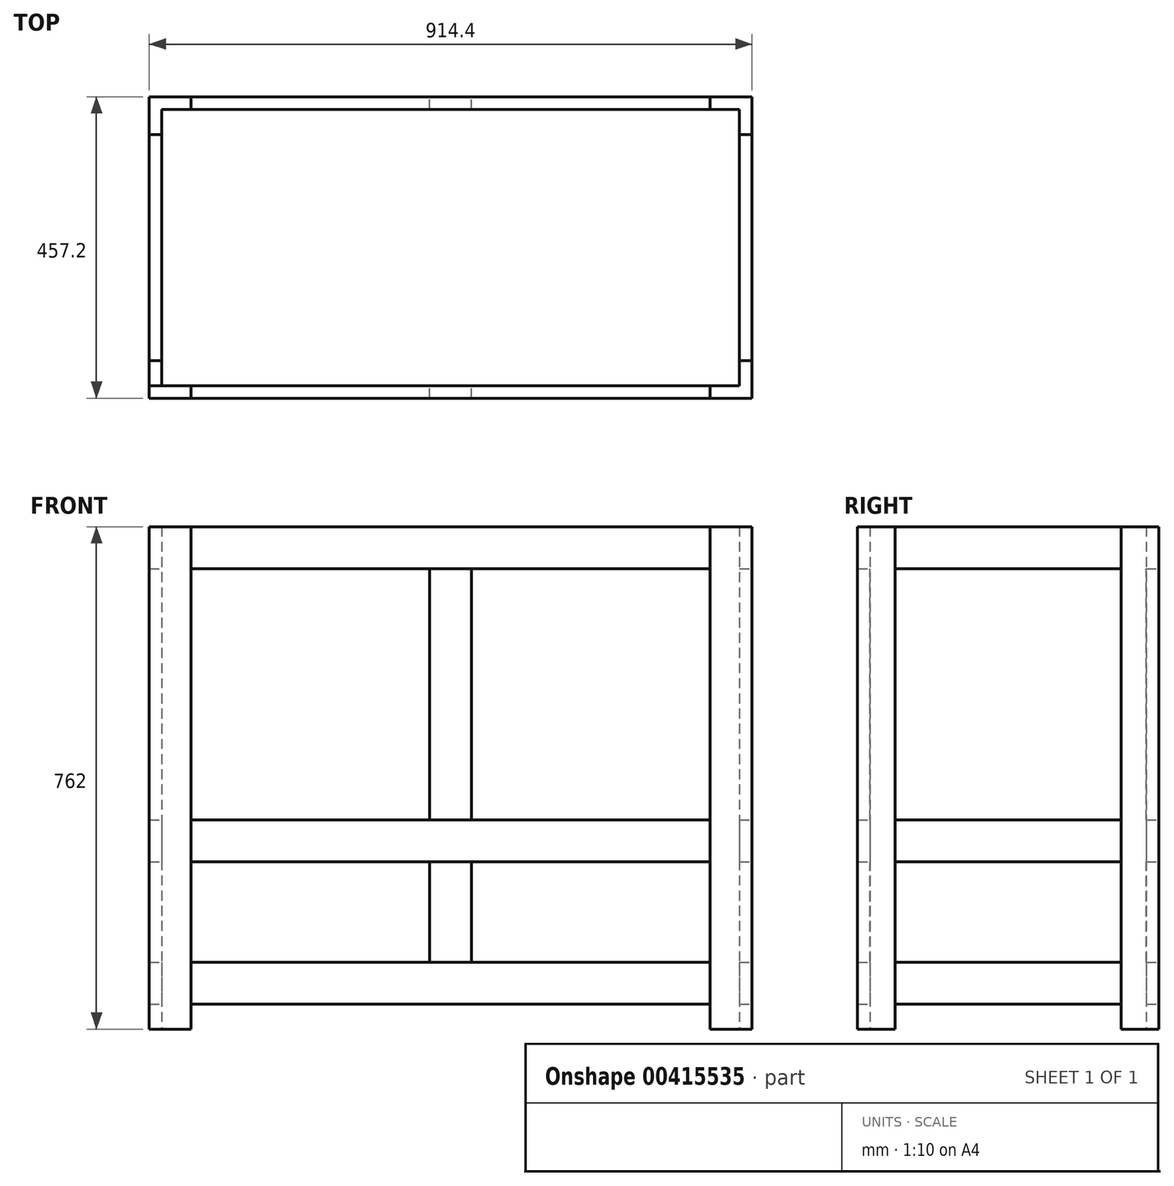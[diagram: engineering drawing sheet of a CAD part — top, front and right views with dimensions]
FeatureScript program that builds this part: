
annotation { "Feature Type Name" : "Feature", "Feature Type Description" : "" }
export const myFeature = defineFeature(function(context is Context, id is Id, definition is map)
    precondition{}
    {
        {
            var Q0;
            Q0=qCreatedBy(makeId("Top.planeOp"),FACE);
            var sketch = newSketch(context, id + "F0", { "sketchPlane" : qUnion([Q0])});
            skLineSegment(sketch, "E0.bottom", {"start": v(0, 0) * mm, "end": v(63.5, 0) * mm});
            skLineSegment(sketch, "E0.top", {"start": v(0, -19.05) * mm, "end": v(63.5, -19.05) * mm});
            skLineSegment(sketch, "E0.left", {"start": v(0, 0) * mm, "end": v(0, -19.05) * mm});
            skLineSegment(sketch, "E0.right", {"start": v(63.5, 0) * mm, "end": v(63.5, -19.05) * mm});
            skSolve(sketch);
        }
        {
            var Q0;
            Q0 = qSketchRegion(id + "F0", true);
            extrude(context, id + "F1", {"entities" : qUnion([Q0]), "depth" : 762 * mm});
        }
        {
            var Q0;
            Q0=qCreatedBy(makeId("Top.planeOp"),FACE);
            var sketch = newSketch(context, id + "F2", { "sketchPlane" : qUnion([Q0])});
            skLineSegment(sketch, "E1.bottom", {"start": v(0, -19.05) * mm, "end": v(19.05, -19.05) * mm});
            skLineSegment(sketch, "E1.top", {"start": v(0, -57.15) * mm, "end": v(19.05, -57.15) * mm});
            skLineSegment(sketch, "E1.left", {"start": v(0, -19.05) * mm, "end": v(0, -57.15) * mm});
            skLineSegment(sketch, "E1.right", {"start": v(19.05, -19.05) * mm, "end": v(19.05, -57.15) * mm});
            skSolve(sketch);
        }
        {
            var Q0;
            Q0 = qSketchRegion(id + "F2", true);
            extrude(context, id + "F3", {"entities" : qUnion([Q0]), "operationType" : NewBodyOperationType.ADD, "depth" : 762 * mm});
        }
        {
            var Q0;
            Q0=qCreatedBy(makeId("Top.planeOp"),FACE);
            var sketch = newSketch(context, id + "F4", { "sketchPlane" : qUnion([Q0])});
            skLineSegment(sketch, "E2.bottom", {"start": v(0, -438.15) * mm, "end": v(63.5, -438.15) * mm});
            skLineSegment(sketch, "E2.top", {"start": v(0, -457.2) * mm, "end": v(63.5, -457.2) * mm});
            skLineSegment(sketch, "E2.left", {"start": v(0, -438.15) * mm, "end": v(0, -457.2) * mm});
            skLineSegment(sketch, "E2.right", {"start": v(63.5, -438.15) * mm, "end": v(63.5, -457.2) * mm});
            skSolve(sketch);
        }
        {
            var Q0;
            Q0=qCreatedBy(makeId("Top.planeOp"),FACE);
            var sketch = newSketch(context, id + "F5", { "sketchPlane" : qUnion([Q0])});
            skLineSegment(sketch, "E3.bottom", {"start": v(19.05, -400.05) * mm, "end": v(0, -400.05) * mm});
            skLineSegment(sketch, "E3.top", {"start": v(19.05, -438.15) * mm, "end": v(0, -438.15) * mm});
            skLineSegment(sketch, "E3.left", {"start": v(19.05, -400.05) * mm, "end": v(19.05, -438.15) * mm});
            skLineSegment(sketch, "E3.right", {"start": v(0, -400.05) * mm, "end": v(0, -438.15) * mm});
            skSolve(sketch);
        }
        {
            var Q0;
            Q0=qCreatedBy(makeId("Top.planeOp"),FACE);
            var sketch = newSketch(context, id + "F6", { "sketchPlane" : qUnion([Q0])});
            skLineSegment(sketch, "E4.bottom", {"start": v(850.9, 0) * mm, "end": v(914.4, 0) * mm});
            skLineSegment(sketch, "E4.top", {"start": v(850.9, -19.05) * mm, "end": v(914.4, -19.05) * mm});
            skLineSegment(sketch, "E4.left", {"start": v(850.9, 0) * mm, "end": v(850.9, -19.05) * mm});
            skLineSegment(sketch, "E4.right", {"start": v(914.4, 0) * mm, "end": v(914.4, -19.05) * mm});
            skSolve(sketch);
        }
        {
            var Q0;
            Q0=qCreatedBy(makeId("Top.planeOp"),FACE);
            var sketch = newSketch(context, id + "F7", { "sketchPlane" : qUnion([Q0])});
            skLineSegment(sketch, "E5.bottom", {"start": v(895.35, -57.15) * mm, "end": v(914.4, -57.15) * mm});
            skLineSegment(sketch, "E5.top", {"start": v(895.35, -19.05) * mm, "end": v(914.4, -19.05) * mm});
            skLineSegment(sketch, "E5.left", {"start": v(895.35, -57.15) * mm, "end": v(895.35, -19.05) * mm});
            skLineSegment(sketch, "E5.right", {"start": v(914.4, -57.15) * mm, "end": v(914.4, -19.05) * mm});
            skSolve(sketch);
        }
        {
            var Q0;
            Q0=qCreatedBy(makeId("Top.planeOp"),FACE);
            var sketch = newSketch(context, id + "F8", { "sketchPlane" : qUnion([Q0])});
            skLineSegment(sketch, "E6.bottom", {"start": v(850.9, -457.2) * mm, "end": v(914.4, -457.2) * mm});
            skLineSegment(sketch, "E6.top", {"start": v(850.9, -438.15) * mm, "end": v(914.4, -438.15) * mm});
            skLineSegment(sketch, "E6.left", {"start": v(850.9, -457.2) * mm, "end": v(850.9, -438.15) * mm});
            skLineSegment(sketch, "E6.right", {"start": v(914.4, -457.2) * mm, "end": v(914.4, -438.15) * mm});
            skSolve(sketch);
        }
        {
            var Q0;
            Q0=qCreatedBy(makeId("Top.planeOp"),FACE);
            var sketch = newSketch(context, id + "F9", { "sketchPlane" : qUnion([Q0])});
            skLineSegment(sketch, "E7.bottom", {"start": v(895.35, -400.05) * mm, "end": v(914.4, -400.05) * mm});
            skLineSegment(sketch, "E7.top", {"start": v(895.35, -438.15) * mm, "end": v(914.4, -438.15) * mm});
            skLineSegment(sketch, "E7.left", {"start": v(895.35, -400.05) * mm, "end": v(895.35, -438.15) * mm});
            skLineSegment(sketch, "E7.right", {"start": v(914.4, -400.05) * mm, "end": v(914.4, -438.15) * mm});
            skSolve(sketch);
        }
        {
            var Q0;
            Q0 = qSketchRegion(id + "F4", true);
            extrude(context, id + "F10", {"entities" : qUnion([Q0]), "depth" : 762 * mm});
        }
        {
            var Q0;
            Q0 = qSketchRegion(id + "F5", true);
            extrude(context, id + "F11", {"entities" : qUnion([Q0]), "depth" : 762 * mm});
        }
        {
            var Q0;
            Q0 = qSketchRegion(id + "F6", true);
            extrude(context, id + "F12", {"entities" : qUnion([Q0]), "depth" : 762 * mm});
        }
        {
            var Q0;
            Q0 = qSketchRegion(id + "F7", true);
            extrude(context, id + "F13", {"entities" : qUnion([Q0]), "operationType" : NewBodyOperationType.ADD, "depth" : 762 * mm});
        }
        {
            var Q0;
            Q0 = qSketchRegion(id + "F8", true);
            extrude(context, id + "F14", {"entities" : qUnion([Q0]), "depth" : 762 * mm});
        }
        {
            var Q0;
            Q0 = qSketchRegion(id + "F9", true);
            extrude(context, id + "F15", {"entities" : qUnion([Q0]), "operationType" : NewBodyOperationType.ADD, "depth" : 762 * mm});
        }
        {
            var Q0;
            Q0=makeQuery(id+"F10.opExtrude","SWEPT_FACE",FACE,{"disambiguationData":[OSD([sQuery(id+"F4.wireOp",EDGE,"E2.right")])]});
            var sketch = newSketch(context, id + "F16", { "sketchPlane" : qUnion([Q0])});
            skLineSegment(sketch, "E8.bottom", {"start": v(-457.2, 762) * mm, "end": v(-438.15, 762) * mm});
            skLineSegment(sketch, "E8.top", {"start": v(-457.2, 698.5) * mm, "end": v(-438.15, 698.5) * mm});
            skLineSegment(sketch, "E8.left", {"start": v(-457.2, 762) * mm, "end": v(-457.2, 698.5) * mm});
            skLineSegment(sketch, "E8.right", {"start": v(-438.15, 762) * mm, "end": v(-438.15, 698.5) * mm});
            skLineSegment(sketch, "E9.bottom", {"start": v(-457.2, 317.5) * mm, "end": v(-438.15, 317.5) * mm});
            skLineSegment(sketch, "E9.top", {"start": v(-457.2, 254) * mm, "end": v(-438.15, 254) * mm});
            skLineSegment(sketch, "E9.left", {"start": v(-457.2, 317.5) * mm, "end": v(-457.2, 254) * mm});
            skLineSegment(sketch, "E9.right", {"start": v(-438.15, 317.5) * mm, "end": v(-438.15, 254) * mm});
            skLineSegment(sketch, "E10.bottom", {"start": v(-457.2, 101.6) * mm, "end": v(-438.15, 101.6) * mm});
            skLineSegment(sketch, "E10.top", {"start": v(-457.2, 38.1) * mm, "end": v(-438.15, 38.1) * mm});
            skLineSegment(sketch, "E10.left", {"start": v(-457.2, 101.6) * mm, "end": v(-457.2, 38.1) * mm});
            skLineSegment(sketch, "E10.right", {"start": v(-438.15, 101.6) * mm, "end": v(-438.15, 38.1) * mm});
            skSolve(sketch);
        }
        {
            var Q0;
            Q0 = qSketchRegion(id + "F16", true);
            extrude(context, id + "F17", {"entities" : qUnion([Q0]), "depth" : 787.4 * mm});
        }
        {
            var Q0;
            Q0=makeQuery(id+"F1.opExtrude","SWEPT_FACE",FACE,{"disambiguationData":[OSD([sQuery(id+"F0.wireOp",EDGE,"E0.right")])]});
            var sketch = newSketch(context, id + "F18", { "sketchPlane" : qUnion([Q0])});
            skLineSegment(sketch, "E11.bottom", {"start": v(-19.05, 762) * mm, "end": v(0, 762) * mm});
            skLineSegment(sketch, "E11.top", {"start": v(-19.05, 698.5) * mm, "end": v(0, 698.5) * mm});
            skLineSegment(sketch, "E11.left", {"start": v(-19.05, 762) * mm, "end": v(-19.05, 698.5) * mm});
            skLineSegment(sketch, "E11.right", {"start": v(0, 762) * mm, "end": v(0, 698.5) * mm});
            skLineSegment(sketch, "E12.bottom", {"start": v(-19.05, 317.5) * mm, "end": v(0, 317.5) * mm});
            skLineSegment(sketch, "E12.top", {"start": v(-19.05, 254) * mm, "end": v(0, 254) * mm});
            skLineSegment(sketch, "E12.left", {"start": v(-19.05, 317.5) * mm, "end": v(-19.05, 254) * mm});
            skLineSegment(sketch, "E12.right", {"start": v(0, 317.5) * mm, "end": v(0, 254) * mm});
            skLineSegment(sketch, "E13.bottom", {"start": v(-19.05, 101.6) * mm, "end": v(0, 101.6) * mm});
            skLineSegment(sketch, "E13.top", {"start": v(-19.05, 38.1) * mm, "end": v(0, 38.1) * mm});
            skLineSegment(sketch, "E13.left", {"start": v(-19.05, 101.6) * mm, "end": v(-19.05, 38.1) * mm});
            skLineSegment(sketch, "E13.right", {"start": v(0, 101.6) * mm, "end": v(0, 38.1) * mm});
            skSolve(sketch);
        }
        {
            var Q0;
            Q0 = qSketchRegion(id + "F18", true);
            extrude(context, id + "F19", {"entities" : qUnion([Q0]), "depth" : 787.4 * mm});
        }
        {
            var Q0;
            Q0=makeQuery(id+"F13.opExtrude","SWEPT_FACE",FACE,{"disambiguationData":[OSD([sQuery(id+"F7.wireOp",EDGE,"E5.bottom")])]});
            var sketch = newSketch(context, id + "F20", { "sketchPlane" : qUnion([Q0])});
            skLineSegment(sketch, "E14.bottom", {"start": v(895.35, 762) * mm, "end": v(914.4, 762) * mm});
            skLineSegment(sketch, "E14.top", {"start": v(895.35, 698.5) * mm, "end": v(914.4, 698.5) * mm});
            skLineSegment(sketch, "E14.left", {"start": v(895.35, 762) * mm, "end": v(895.35, 698.5) * mm});
            skLineSegment(sketch, "E14.right", {"start": v(914.4, 762) * mm, "end": v(914.4, 698.5) * mm});
            skLineSegment(sketch, "E15.bottom", {"start": v(895.35, 317.5) * mm, "end": v(914.4, 317.5) * mm});
            skLineSegment(sketch, "E15.top", {"start": v(895.35, 254) * mm, "end": v(914.4, 254) * mm});
            skLineSegment(sketch, "E15.left", {"start": v(895.35, 317.5) * mm, "end": v(895.35, 254) * mm});
            skLineSegment(sketch, "E15.right", {"start": v(914.4, 317.5) * mm, "end": v(914.4, 254) * mm});
            skLineSegment(sketch, "E16.bottom", {"start": v(895.35, 101.6) * mm, "end": v(914.4, 101.6) * mm});
            skLineSegment(sketch, "E16.top", {"start": v(895.35, 38.1) * mm, "end": v(914.4, 38.1) * mm});
            skLineSegment(sketch, "E16.left", {"start": v(895.35, 101.6) * mm, "end": v(895.35, 38.1) * mm});
            skLineSegment(sketch, "E16.right", {"start": v(914.4, 101.6) * mm, "end": v(914.4, 38.1) * mm});
            skSolve(sketch);
        }
        {
            var Q0;
            Q0 = qSketchRegion(id + "F20", true);
            extrude(context, id + "F21", {"entities" : qUnion([Q0]), "depth" : 342.9 * mm});
        }
        {
            var Q0;
            Q0=makeQuery(id+"F3.opExtrude","SWEPT_FACE",FACE,{"disambiguationData":[OSD([sQuery(id+"F2.wireOp",EDGE,"E1.top")])]});
            var sketch = newSketch(context, id + "F22", { "sketchPlane" : qUnion([Q0])});
            skLineSegment(sketch, "E17.bottom", {"start": v(0, 762) * mm, "end": v(19.05, 762) * mm});
            skLineSegment(sketch, "E17.top", {"start": v(0, 698.5) * mm, "end": v(19.05, 698.5) * mm});
            skLineSegment(sketch, "E17.left", {"start": v(0, 762) * mm, "end": v(0, 698.5) * mm});
            skLineSegment(sketch, "E17.right", {"start": v(19.05, 762) * mm, "end": v(19.05, 698.5) * mm});
            skLineSegment(sketch, "E18.bottom", {"start": v(0, 317.5) * mm, "end": v(19.05, 317.5) * mm});
            skLineSegment(sketch, "E18.top", {"start": v(0, 254) * mm, "end": v(19.05, 254) * mm});
            skLineSegment(sketch, "E18.left", {"start": v(0, 317.5) * mm, "end": v(0, 254) * mm});
            skLineSegment(sketch, "E18.right", {"start": v(19.05, 317.5) * mm, "end": v(19.05, 254) * mm});
            skLineSegment(sketch, "E19.bottom", {"start": v(0, 101.6) * mm, "end": v(19.05, 101.6) * mm});
            skLineSegment(sketch, "E19.top", {"start": v(0, 38.1) * mm, "end": v(19.05, 38.1) * mm});
            skLineSegment(sketch, "E19.left", {"start": v(0, 101.6) * mm, "end": v(0, 38.1) * mm});
            skLineSegment(sketch, "E19.right", {"start": v(19.05, 101.6) * mm, "end": v(19.05, 38.1) * mm});
            skSolve(sketch);
        }
        {
            var Q0;
            Q0 = qSketchRegion(id + "F22", true);
            extrude(context, id + "F23", {"entities" : qUnion([Q0]), "depth" : 342.9 * mm});
        }
        {
            var Q0;
            Q0=makeQuery(id+"F17.opExtrude","SWEPT_FACE",FACE,{"disambiguationData":[OSD([sQuery(id+"F16.wireOp",EDGE,"E8.top")])]});
            var sketch = newSketch(context, id + "F24", { "sketchPlane" : qUnion([Q0])});
            skLineSegment(sketch, "E20.bottom", {"start": v(425.45, 457.2) * mm, "end": v(488.95, 457.2) * mm});
            skLineSegment(sketch, "E20.top", {"start": v(425.45, 438.15) * mm, "end": v(488.95, 438.15) * mm});
            skLineSegment(sketch, "E20.left", {"start": v(425.45, 457.2) * mm, "end": v(425.45, 438.15) * mm});
            skLineSegment(sketch, "E20.right", {"start": v(488.95, 457.2) * mm, "end": v(488.95, 438.15) * mm});
            skSolve(sketch);
        }
        {
            var Q0;
            Q0 = qSketchRegion(id + "F24", true);
            extrude(context, id + "F25", {"entities" : qUnion([Q0]), "depth" : 381 * mm});
        }
        {
            var Q0;
            Q0=makeQuery(id+"F19.opExtrude","SWEPT_FACE",FACE,{"disambiguationData":[OSD([sQuery(id+"F18.wireOp",EDGE,"E11.top")])]});
            var sketch = newSketch(context, id + "F26", { "sketchPlane" : qUnion([Q0])});
            skLineSegment(sketch, "E21.bottom", {"start": v(425.45, 19.05) * mm, "end": v(488.95, 19.05) * mm});
            skLineSegment(sketch, "E21.top", {"start": v(425.45, 0) * mm, "end": v(488.95, 0) * mm});
            skLineSegment(sketch, "E21.left", {"start": v(425.45, 19.05) * mm, "end": v(425.45, 0) * mm});
            skLineSegment(sketch, "E21.right", {"start": v(488.95, 19.05) * mm, "end": v(488.95, 0) * mm});
            skSolve(sketch);
        }
        {
            var Q0;
            Q0 = qSketchRegion(id + "F26", true);
            extrude(context, id + "F27", {"entities" : qUnion([Q0]), "depth" : 381 * mm});
        }
        {
            var Q0;
            Q0=makeQuery(id+"F17.opExtrude","SWEPT_FACE",FACE,{"disambiguationData":[OSD([sQuery(id+"F16.wireOp",EDGE,"E9.top")])]});
            var sketch = newSketch(context, id + "F28", { "sketchPlane" : qUnion([Q0])});
            skLineSegment(sketch, "E22.bottom", {"start": v(425.45, 457.2) * mm, "end": v(488.95, 457.2) * mm});
            skLineSegment(sketch, "E22.top", {"start": v(425.45, 438.15) * mm, "end": v(488.95, 438.15) * mm});
            skLineSegment(sketch, "E22.left", {"start": v(425.45, 457.2) * mm, "end": v(425.45, 438.15) * mm});
            skLineSegment(sketch, "E22.right", {"start": v(488.95, 457.2) * mm, "end": v(488.95, 438.15) * mm});
            skSolve(sketch);
        }
        {
            var Q0;
            Q0 = qSketchRegion(id + "F28", true);
            extrude(context, id + "F29", {"entities" : qUnion([Q0]), "depth" : 152.4 * mm});
        }
        {
            var Q0;
            Q0=makeQuery(id+"F19.opExtrude","SWEPT_FACE",FACE,{"disambiguationData":[OSD([sQuery(id+"F18.wireOp",EDGE,"E12.top")])]});
            var sketch = newSketch(context, id + "F30", { "sketchPlane" : qUnion([Q0])});
            skLineSegment(sketch, "E23.bottom", {"start": v(425.45, 19.05) * mm, "end": v(488.95, 19.05) * mm});
            skLineSegment(sketch, "E23.top", {"start": v(425.45, 0) * mm, "end": v(488.95, 0) * mm});
            skLineSegment(sketch, "E23.left", {"start": v(425.45, 19.05) * mm, "end": v(425.45, 0) * mm});
            skLineSegment(sketch, "E23.right", {"start": v(488.95, 19.05) * mm, "end": v(488.95, 0) * mm});
            skSolve(sketch);
        }
        {
            var Q0;
            Q0 = qSketchRegion(id + "F30", true);
            extrude(context, id + "F31", {"entities" : qUnion([Q0]), "depth" : 152.4 * mm});
        }
    });
